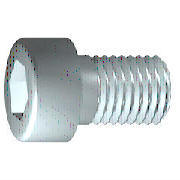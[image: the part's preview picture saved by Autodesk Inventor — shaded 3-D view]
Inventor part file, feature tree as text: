
AUTODESK INVENTOR PART (.ipt)
format: ipt  version: 2017.1 (Build 211199000, 199)  size: 194,048 bytes
history: native  units: mm (DEFAULTED — no unit token found)
features: sketch x2, extrude x1, plane x1, fillet x1
ambient origin geometry x7: Origin, YZ Plane, XY Plane, X Axis, Y Axis, Z Axis, Center Point
bodies: Solid1 (feature_tree), Body (feature_tree)
feature tree (5):
  extrude  "Slot"  Depth=4.826mm
  plane  "Work Plane1"
  fillet  "Fillet2"  Radius=4.826mm
  sketch  "Sketch1"  dims[d1=10.053882mm d2=2.646018mm d3=4.826mm]
  sketch  "Sketch2"  dims[d4=2.286mm d5=60.0deg d6=4.826mm d7=4.826mm d8=4.575385mm d9=7.9248mm d10=90.0deg d11=10.0mm d12=0.0mm d13=10.053882mm d14=0.0mm d15=0.62992mm d16=0.62992mm d17=0.4572mm d19=0.0mm d26=12.7mm d27=45.0deg d28=0.0mm d29=0.0mm d30=0.1524mm]
